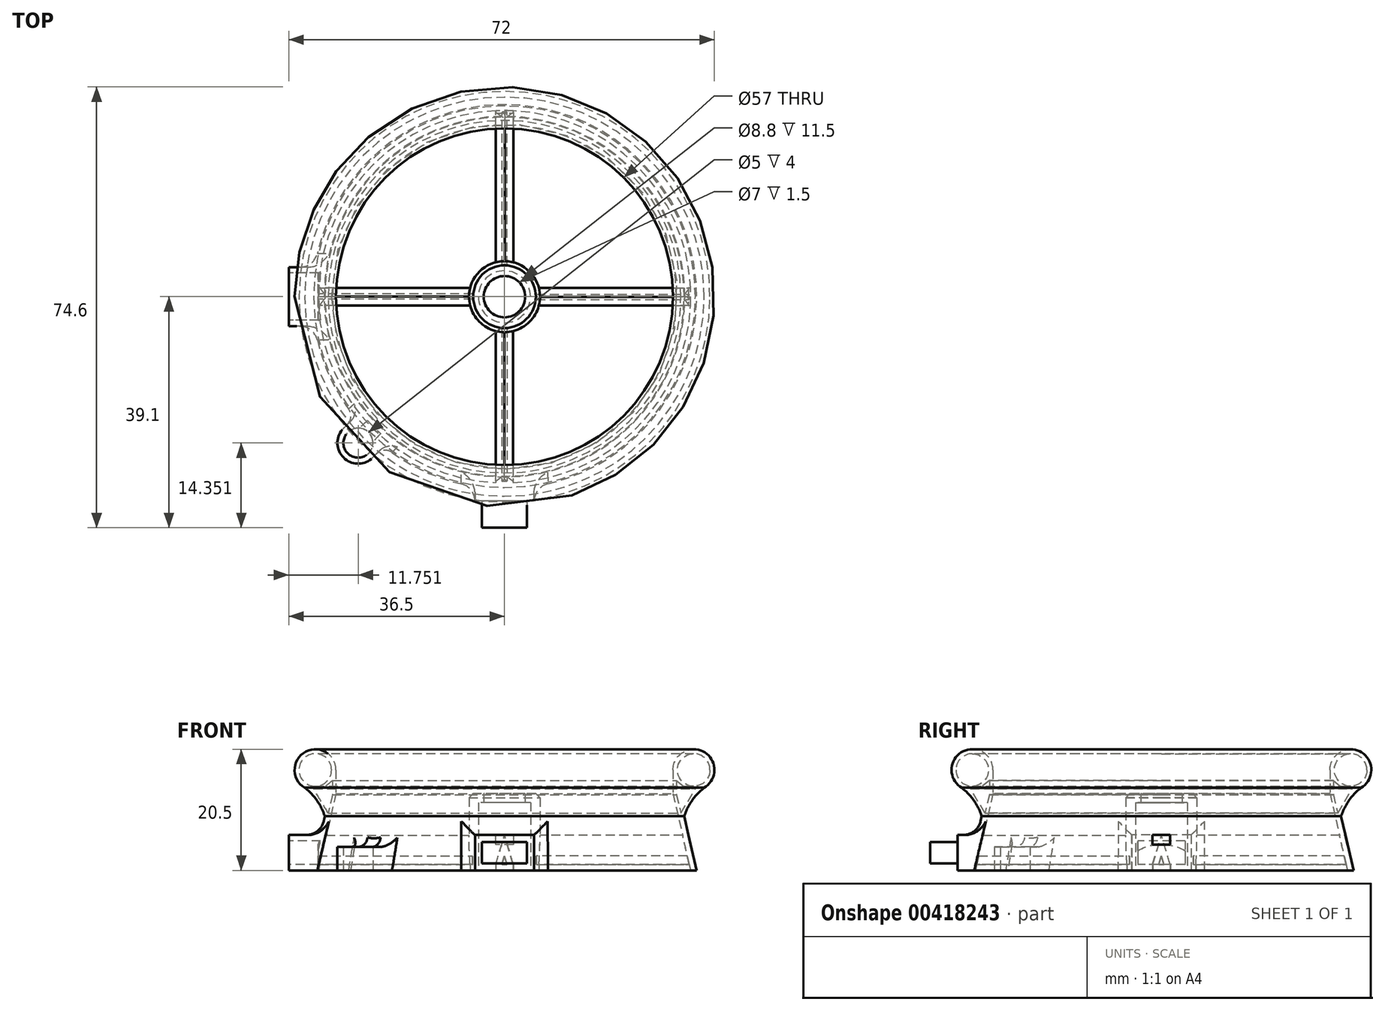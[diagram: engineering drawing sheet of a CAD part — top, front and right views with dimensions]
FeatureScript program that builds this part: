
annotation { "Feature Type Name" : "Feature", "Feature Type Description" : "" }
export const myFeature = defineFeature(function(context is Context, id is Id, definition is map)
    precondition{}
    {
        {
            var Q0;
            Q0=qCreatedBy(makeId("Top.planeOp"),FACE);
            var sketch = newSketch(context, id + "F0", { "sketchPlane" : qUnion([Q0])});
            skCircle(sketch, "E0", {"center": v(0, 0) * mm, "radius": 31.5 * mm});
            skCircle(sketch, "E1", {"center": v(0, 0) * mm, "radius": 4.4 * mm});
            skCircle(sketch, "E2", {"center": v(0, 0) * mm, "radius": 6 * mm});
            skLineSegment(sketch, "E3", {"start": v(5.82, 1.46) * mm, "end": v(31.47, 1.46) * mm});
            skLineSegment(sketch, "E4.MirrorCS", {"start": v(5.8, -1.5) * mm, "end": v(31.46, -1.5) * mm});
            skLineSegment(sketch, "E5.1.0", {"start": v(-1.46, 5.82) * mm, "end": v(-1.46, 31.47) * mm});
            skLineSegment(sketch, "E5.1.1", {"start": v(1.5, 5.8) * mm, "end": v(1.5, 31.46) * mm});
            skLineSegment(sketch, "E5.2.0", {"start": v(-5.82, -1.46) * mm, "end": v(-31.47, -1.46) * mm});
            skLineSegment(sketch, "E5.2.1", {"start": v(-5.8, 1.5) * mm, "end": v(-31.46, 1.5) * mm});
            skLineSegment(sketch, "E5.3.0", {"start": v(1.46, -5.82) * mm, "end": v(1.46, -31.47) * mm});
            skLineSegment(sketch, "E5.3.1", {"start": v(-1.5, -5.8) * mm, "end": v(-1.5, -31.46) * mm});
            skPoint(sketch, "E6.orphan", {"position": v(28.46, -1.5) * mm});
            skPoint(sketch, "E7.orphan", {"position": v(1.5, 28.46) * mm});
            skLineSegment(sketch, "E8", {"start": v(-31.1, 5) * mm, "end": v(-36.5, 5) * mm});
            skLineSegment(sketch, "E9.MirrorCS", {"start": v(-31.1, -5) * mm, "end": v(-36.5, -5) * mm});
            skLineSegment(sketch, "E10", {"start": v(-36.5, 5) * mm, "end": v(-36.5, -5) * mm});
            skPoint(sketch, "E11", {"position": v(-31.5, 0) * mm});
            skPoint(sketch, "E12", {"position": v(0, -31.5) * mm});
            skLineSegment(sketch, "E13", {"start": v(-5, -34.5) * mm, "end": v(-5, -31.1) * mm});
            skLineSegment(sketch, "E14.MirrorCS", {"start": v(5, -34.5) * mm, "end": v(5, -31.1) * mm});
            skLineSegment(sketch, "E15", {"start": v(-5, -34.5) * mm, "end": v(5, -34.5) * mm});
            skLineSegment(sketch, "E16", {"start": v(-3.8, -34.5) * mm, "end": v(-3.8, -39.1) * mm});
            skLineSegment(sketch, "E17.MirrorCS", {"start": v(3.8, -34.5) * mm, "end": v(3.8, -39.1) * mm});
            skLineSegment(sketch, "E18", {"start": v(-3.8, -39.1) * mm, "end": v(3.8, -39.1) * mm});
            skLineSegment(sketch, "E19", {"start": v(0, 0) * mm, "end": v(-4.24, -4.24) * mm});
            skPoint(sketch, "E20", {"position": v(-22.27, -22.27) * mm});
            skCircle(sketch, "E21", {"center": v(-24.75, -24.75) * mm, "radius": 2.5 * mm});
            skArc(sketch, "E22", {"start": v(-27.22, -22.27) * mm, "mid": v(-27.22, -27.22) * mm, "end": v(-22.27, -27.22) * mm});
            skPoint(sketch, "E23", {"position": v(-22.27, -27.22) * mm});
            skPoint(sketch, "E24", {"position": v(-27.22, -22.27) * mm});
            skLineSegment(sketch, "E25", {"start": v(-22.27, -27.22) * mm, "end": v(-19.66, -24.61) * mm});
            skLineSegment(sketch, "E26", {"start": v(-27.22, -22.27) * mm, "end": v(-24.61, -19.66) * mm});
            skSolve(sketch);
        }
        {
            var Q0;
            Q0=qCreatedBy(makeId("Front.planeOp"),FACE);
            var sketch = newSketch(context, id + "F1", { "sketchPlane" : qUnion([Q0])});
            skLineSegment(sketch, "E27", {"start": v(-27.5, 0) * mm, "end": v(-27.5, 17) * mm});
            skLineSegment(sketch, "E28", {"start": v(-28.5, 17) * mm, "end": v(-28.5, 13) * mm});
            skLineSegment(sketch, "E29", {"start": v(-28.5, 13) * mm, "end": v(-31.5, 0) * mm});
            skPoint(sketch, "E30.orphan", {"position": v(-28.5, 0) * mm});
            skArc(sketch, "E31", {"start": v(-28.5, 17) * mm, "mid": v(-33.74, 20.04) * mm, "end": v(-33.77, 13.98) * mm});
            skLineSegment(sketch, "E32", {"start": v(-31.5, 0) * mm, "end": v(-32.5, 0) * mm});
            skLineSegment(sketch, "E33", {"start": v(-32.5, 0) * mm, "end": v(-30.39, 9.15) * mm});
            skCircle(sketch, "E34", {"center": v(-32, 17) * mm, "radius": 2.75 * mm});
            skArc(sketch, "E35", {"start": v(-30.39, 9.15) * mm, "mid": v(-31.71, 11.82) * mm, "end": v(-33.77, 13.98) * mm});
            skLineSegment(sketch, "E36", {"start": v(-32.28, 13.8) * mm, "end": v(-29.83, 9.72) * mm});
            skLineSegment(sketch, "E37", {"start": v(-29.83, 9.72) * mm, "end": v(-29.08, 12.78) * mm});
            skLineSegment(sketch, "E38", {"start": v(-29.08, 12.78) * mm, "end": v(-29.08, 15.2) * mm});
            skLineSegment(sketch, "E39", {"start": v(-29.08, 15.2) * mm, "end": v(-30.51, 14.08) * mm});
            skLineSegment(sketch, "E40", {"start": v(-30.51, 14.08) * mm, "end": v(-32.28, 13.8) * mm});
            skLineSegment(sketch, "E41", {"start": v(-27.5, 0) * mm, "end": v(0, 0) * mm});
            skSolve(sketch);
        }
        {
            var Q0;
            Q0=makeQuery(id+"F1.imprint","IMPRINT",FACE,{"disambiguationData":[TD([[makeQuery(id+"F1.imprint","IMPRINT",EDGE,{"derivedFrom":sQuery(id+"F1.wireOp",EDGE,"E28")}),-1.0]])]});
            var Q1;
            Q1=sQuery(id+"F0.wireOp",EDGE,"E0");
            revolve(context, id + "F2", {"entities" : qUnion([Q0]), "axis" : qUnion([Q1]), "revolveType" : RevolveType.FULL});
        }
        {
            var Q0;
            {var subQ0=sQuery(id+"F0.wireOp",EDGE,"E5.2.0");Q0=makeQuery(id+"F0.imprint","IMPRINT",FACE,{"disambiguationData":[TD([[makeQuery(id+"F0.imprint","IMPRINT",EDGE,{"derivedFrom":subQ0}),-1.0]])]});}
            var Q1;
            {var subQ0=sQuery(id+"F0.wireOp",EDGE,"E5.3.0");Q1=makeQuery(id+"F0.imprint","IMPRINT",FACE,{"disambiguationData":[TD([[makeQuery(id+"F0.imprint","IMPRINT",EDGE,{"derivedFrom":subQ0}),-1.0]])]});}
            var Q2;
            {var subQ0=sQuery(id+"F0.wireOp",EDGE,"E3");Q2=makeQuery(id+"F0.imprint","IMPRINT",FACE,{"disambiguationData":[TD([[makeQuery(id+"F0.imprint","IMPRINT",EDGE,{"derivedFrom":subQ0}),-1.0]])]});}
            var Q3;
            {var subQ0=sQuery(id+"F0.wireOp",EDGE,"E5.1.0");Q3=makeQuery(id+"F0.imprint","IMPRINT",FACE,{"disambiguationData":[TD([[makeQuery(id+"F0.imprint","IMPRINT",EDGE,{"derivedFrom":subQ0}),-1.0]])]});}
            extrude(context, id + "F3", {"entities" : qUnion([Q0, Q1, Q2, Q3]), "operationType" : NewBodyOperationType.ADD, "depth" : 6 * mm});
        }
        {
            var Q0;
            Q0=makeQuery(id+"F0.imprint","IMPRINT",FACE,{"disambiguationData":[TD([[makeQuery(id+"F0.imprint","IMPRINT",EDGE,{"derivedFrom":sQuery(id+"F0.wireOp",EDGE,"E1")}),-1.0]])]});
            extrude(context, id + "F4", {"entities" : qUnion([Q0]), "operationType" : NewBodyOperationType.ADD, "depth" : 11.5 * mm});
        }
        {
            var Q0;
            {var subQ1=sQuery(id+"F0.wireOp",EDGE,"E5.3.0");Q0=makeQuery(id+"F3.boolean.opBoolean","SPLIT",EDGE,{"disambiguationData":[TD([makeQuery(id+"F2.opRevolve","SWEPT_FACE",FACE,{"disambiguationData":[OSD([sQuery(id+"F1.wireOp",EDGE,"E29")])]})])],"derivedFrom":makeQuery(id+"F3.opExtrude","CAP_EDGE",EDGE,{"disambiguationData":[OSD([subQ1])],"isStart":false})});}
            var Q1;
            {var subQ0=sQuery(id+"F0.wireOp",EDGE,"E3");Q1=makeQuery(id+"F3.boolean.opBoolean","SPLIT",EDGE,{"disambiguationData":[TD([makeQuery(id+"F2.opRevolve","SWEPT_FACE",FACE,{"disambiguationData":[OSD([sQuery(id+"F1.wireOp",EDGE,"E29")])]})])],"derivedFrom":makeQuery(id+"F3.opExtrude","CAP_EDGE",EDGE,{"disambiguationData":[OSD([subQ0])],"isStart":false})});}
            var Q2;
            {var subQ1=sQuery(id+"F0.wireOp",EDGE,"E5.1.0");Q2=makeQuery(id+"F3.boolean.opBoolean","SPLIT",EDGE,{"disambiguationData":[TD([makeQuery(id+"F2.opRevolve","SWEPT_FACE",FACE,{"disambiguationData":[OSD([sQuery(id+"F1.wireOp",EDGE,"E29")])]})])],"derivedFrom":makeQuery(id+"F3.opExtrude","CAP_EDGE",EDGE,{"disambiguationData":[OSD([subQ1])],"isStart":false})});}
            var Q3;
            {var subQ1=sQuery(id+"F0.wireOp",EDGE,"E5.2.0");Q3=makeQuery(id+"F3.boolean.opBoolean","SPLIT",EDGE,{"disambiguationData":[TD([makeQuery(id+"F2.opRevolve","SWEPT_FACE",FACE,{"disambiguationData":[OSD([sQuery(id+"F1.wireOp",EDGE,"E29")])]})])],"derivedFrom":makeQuery(id+"F3.opExtrude","CAP_EDGE",EDGE,{"disambiguationData":[OSD([subQ1])],"isStart":false})});}
            chamfer(context, id + "F5", {"entities" : qUnion([Q0, Q1, Q2, Q3]), "chamferType" : ChamferType.TWO_OFFSETS, "width1" : 1.5 * mm, "oppositeDirection" : true, "width2" : 5 * mm, "tangentPropagation" : true});
        }
        {
            var Q0;
            {var subQ2=sQuery(id+"F0.wireOp",EDGE,"E4.MirrorCS");Q0=makeQuery(id+"F3.boolean.opBoolean","SPLIT",EDGE,{"disambiguationData":[TD([makeQuery(id+"F2.opRevolve","SWEPT_FACE",FACE,{"disambiguationData":[OSD([sQuery(id+"F1.wireOp",EDGE,"E29")])]})])],"derivedFrom":makeQuery(id+"F3.opExtrude","CAP_EDGE",EDGE,{"disambiguationData":[OSD([subQ2])],"isStart":false})});}
            var Q1;
            {var subQ0=sQuery(id+"F0.wireOp",EDGE,"E5.1.1");Q1=makeQuery(id+"F3.boolean.opBoolean","SPLIT",EDGE,{"disambiguationData":[TD([makeQuery(id+"F2.opRevolve","SWEPT_FACE",FACE,{"disambiguationData":[OSD([sQuery(id+"F1.wireOp",EDGE,"E29")])]})])],"derivedFrom":makeQuery(id+"F3.opExtrude","CAP_EDGE",EDGE,{"disambiguationData":[OSD([subQ0])],"isStart":false})});}
            var Q2;
            {var subQ0=sQuery(id+"F0.wireOp",EDGE,"E5.3.1");Q2=makeQuery(id+"F3.boolean.opBoolean","SPLIT",EDGE,{"disambiguationData":[TD([makeQuery(id+"F2.opRevolve","SWEPT_FACE",FACE,{"disambiguationData":[OSD([sQuery(id+"F1.wireOp",EDGE,"E29")])]})])],"derivedFrom":makeQuery(id+"F3.opExtrude","CAP_EDGE",EDGE,{"disambiguationData":[OSD([subQ0])],"isStart":false})});}
            var Q3;
            {var subQ0=sQuery(id+"F0.wireOp",EDGE,"E5.2.1");Q3=makeQuery(id+"F3.boolean.opBoolean","SPLIT",EDGE,{"disambiguationData":[TD([makeQuery(id+"F2.opRevolve","SWEPT_FACE",FACE,{"disambiguationData":[OSD([sQuery(id+"F1.wireOp",EDGE,"E29")])]})])],"derivedFrom":makeQuery(id+"F3.opExtrude","CAP_EDGE",EDGE,{"disambiguationData":[OSD([subQ0])],"isStart":false})});}
            chamfer(context, id + "F6", {"entities" : qUnion([Q0, Q1, Q2, Q3]), "chamferType" : ChamferType.TWO_OFFSETS, "width1" : 5 * mm, "oppositeDirection" : true, "width2" : 1.5 * mm, "tangentPropagation" : true});
        }
        {
            var Q0;
            {var subQ0=sQuery(id+"F0.wireOp",EDGE,"E3");Q0=makeQuery(id+"F3.boolean.opBoolean","SPLIT",FACE,{"disambiguationData":[TD([makeQuery(id+"F2.opRevolve","SWEPT_FACE",FACE,{"disambiguationData":[OSD([sQuery(id+"F1.wireOp",EDGE,"E33")])]})])],"derivedFrom":makeQuery(id+"F3.opExtrude","SWEPT_FACE",FACE,{"disambiguationData":[OSD([subQ0])]})});}
            var Q1;
            Q1=sQuery(id+"F0.wireOp",EDGE,"E0");
            revolve(context, id + "F7", {"operationType" : NewBodyOperationType.REMOVE, "entities" : qUnion([Q0]), "axis" : qUnion([Q1]), "revolveType" : RevolveType.FULL, "oppositeDirection" : true});
        }
        {
            var Q0;
            {var subQ0=sQuery(id+"F0.wireOp",EDGE,"E8");Q0=makeQuery(id+"F0.imprint","IMPRINT",FACE,{"disambiguationData":[TD([[makeQuery(id+"F0.imprint","IMPRINT",EDGE,{"derivedFrom":subQ0}),1.0]])]});}
            extrude(context, id + "F8", {"entities" : qUnion([Q0]), "operationType" : NewBodyOperationType.ADD, "depth" : 6 * mm});
        }
        {
            var Q0;
            Q0=makeQuery(id+"F8.opExtrude","CAP_FACE",FACE,{"disambiguationData":[OSD([sQuery(id+"F0.wireOp",EDGE,"E0"),sQuery(id+"F0.wireOp",EDGE,"E8"),sQuery(id+"F0.wireOp",EDGE,"E9.MirrorCS"),sQuery(id+"F0.wireOp",EDGE,"E10")])],"isStart":false});
            var sketch = newSketch(context, id + "F9", { "sketchPlane" : qUnion([Q0])});
            skLineSegment(sketch, "E42", {"start": v(-34.09, 5) * mm, "end": v(-34.09, -5) * mm});
            skSolve(sketch);
        }
        {
            var Q0;
            {var subQ0=sQuery(id+"F9.wireOp",EDGE,"E42");Q0=makeQuery(id+"F9.imprint","IMPRINT",FACE,{"disambiguationData":[TD([[makeQuery(id+"F9.imprint","IMPRINT",EDGE,{"derivedFrom":subQ0}),1.0]])]});}
            extrude(context, id + "F10", {"entities" : qUnion([Q0]), "operationType" : NewBodyOperationType.REMOVE, "oppositeDirection" : true, "depth" : 2 * mm});
        }
        {
            var Q0;
            Q0=makeQuery(id+"F10.boolean.opBoolean","COPY",FACE,{"derivedFrom":makeQuery(id+"F10.opExtrude","SWEPT_FACE",FACE,{"disambiguationData":[OSD([sQuery(id+"F9.wireOp",EDGE,"E42")])]})});
            var Q1;
            Q1=makeQuery(id+"F2.opRevolve","SWEPT_BODY",BODY,{"disambiguationData":[OSD([sQuery(id+"F1.wireOp",EDGE,"E28"),sQuery(id+"F1.wireOp",EDGE,"E29"),sQuery(id+"F1.wireOp",EDGE,"E31"),sQuery(id+"F1.wireOp",EDGE,"E32"),sQuery(id+"F1.wireOp",EDGE,"E33"),sQuery(id+"F1.wireOp",EDGE,"E34"),sQuery(id+"F1.wireOp",EDGE,"E35"),sQuery(id+"F1.wireOp",EDGE,"E36"),sQuery(id+"F1.wireOp",EDGE,"E37"),sQuery(id+"F1.wireOp",EDGE,"E38"),sQuery(id+"F1.wireOp",EDGE,"E39"),sQuery(id+"F1.wireOp",EDGE,"E40")])]});
            extrude(context, id + "F11", {"entities" : qUnion([Q0]), "operationType" : NewBodyOperationType.ADD, "endBound" : BoundingType.UP_TO_BODY, "endBoundEntityBody" : qUnion([Q1]), "depth" : 25 * mm});
        }
        {
            var Q0;
            Q0=makeQuery(id+"F8.opExtrude","SWEPT_FACE",FACE,{"disambiguationData":[OSD([sQuery(id+"F0.wireOp",EDGE,"E10")])]});
            shell(context, id + "F12", {"entities" : qUnion([Q0]), "thickness" : 1 * mm});
        }
        {
            var Q0;
            {var subQ4=sQuery(id+"F0.wireOp",EDGE,"E13");Q0=makeQuery(id+"F0.imprint","IMPRINT",FACE,{"disambiguationData":[TD([[makeQuery(id+"F0.imprint","IMPRINT",EDGE,{"derivedFrom":subQ4}),-1.0]])]});}
            extrude(context, id + "F13", {"entities" : qUnion([Q0]), "operationType" : NewBodyOperationType.ADD, "depth" : 6 * mm});
        }
        {
            var Q0;
            Q0=makeQuery(id+"F13.opExtrude","CAP_FACE",FACE,{"disambiguationData":[OSD([sQuery(id+"F0.wireOp",EDGE,"E0"),sQuery(id+"F0.wireOp",EDGE,"E13"),sQuery(id+"F0.wireOp",EDGE,"E14.MirrorCS"),sQuery(id+"F0.wireOp",EDGE,"E15")])],"isStart":false});
            var sketch = newSketch(context, id + "F14", { "sketchPlane" : qUnion([Q0])});
            skLineSegment(sketch, "E43", {"start": v(-5, -32.8) * mm, "end": v(5, -32.8) * mm});
            skSolve(sketch);
        }
        {
            var Q0;
            {var subQ0=sQuery(id+"F14.wireOp",EDGE,"E43");Q0=makeQuery(id+"F14.imprint","IMPRINT",FACE,{"disambiguationData":[TD([[makeQuery(id+"F14.imprint","IMPRINT",EDGE,{"derivedFrom":subQ0}),1.0]])]});}
            extrude(context, id + "F15", {"entities" : qUnion([Q0]), "operationType" : NewBodyOperationType.REMOVE, "oppositeDirection" : true, "depth" : 2 * mm});
        }
        {
            var Q0;
            Q0=makeQuery(id+"F15.boolean.opBoolean","COPY",FACE,{"derivedFrom":makeQuery(id+"F15.opExtrude","SWEPT_FACE",FACE,{"disambiguationData":[OSD([sQuery(id+"F14.wireOp",EDGE,"E43")])]})});
            var Q1;
            Q1=makeQuery(id+"F2.opRevolve","SWEPT_BODY",BODY,{"disambiguationData":[OSD([sQuery(id+"F1.wireOp",EDGE,"E28"),sQuery(id+"F1.wireOp",EDGE,"E29"),sQuery(id+"F1.wireOp",EDGE,"E31"),sQuery(id+"F1.wireOp",EDGE,"E32"),sQuery(id+"F1.wireOp",EDGE,"E33"),sQuery(id+"F1.wireOp",EDGE,"E34"),sQuery(id+"F1.wireOp",EDGE,"E35"),sQuery(id+"F1.wireOp",EDGE,"E36"),sQuery(id+"F1.wireOp",EDGE,"E37"),sQuery(id+"F1.wireOp",EDGE,"E38"),sQuery(id+"F1.wireOp",EDGE,"E39"),sQuery(id+"F1.wireOp",EDGE,"E40")])]});
            extrude(context, id + "F16", {"entities" : qUnion([Q0]), "operationType" : NewBodyOperationType.ADD, "endBound" : BoundingType.UP_TO_BODY, "endBoundEntityBody" : qUnion([Q1]), "depth" : 25 * mm});
        }
        {
            var Q0;
            {var subQ0=sQuery(id+"F0.wireOp",EDGE,"E16");Q0=makeQuery(id+"F0.imprint","IMPRINT",FACE,{"disambiguationData":[TD([[makeQuery(id+"F0.imprint","IMPRINT",EDGE,{"derivedFrom":subQ0}),1.0]])]});}
            extrude(context, id + "F17", {"entities" : qUnion([Q0]), "operationType" : NewBodyOperationType.ADD, "depth" : 4.8 * mm, "hasSecondDirection" : true, "secondDirectionOppositeDirection" : false, "secondDirectionDepth" : 1.2 * mm});
        }
        {
            var Q0;
            {var subQ0=sQuery(id+"F0.wireOp",EDGE,"E9.MirrorCS");var subQ1=makeQuery(id+"F2.opRevolve","SWEPT_FACE",FACE,{"disambiguationData":[OSD([sQuery(id+"F1.wireOp",EDGE,"E33")])]});var subQ2=subQ1;var subQ3=makeQuery(id+"F8.opExtrude","SWEPT_FACE",FACE,{"disambiguationData":[OSD([subQ0])]});var subQ4=makeQuery(id+"F8.boolean.opBoolean","INTERSECT",EDGE,{"derivedFrom":[subQ2,subQ3]});Q0=makeQuery(id+"F11.boolean.opBoolean","MERGE",EDGE,{"derivedFrom":[makeQuery(id+"F10.boolean.opBoolean","SPLIT",EDGE,{"disambiguationData":[topologyDisambiguationEdgeConnected([subQ3])],"derivedFrom":subQ4}),makeQuery(id+"F10.boolean.opBoolean","SPLIT",EDGE,{"disambiguationData":[topologyDisambiguationEdgeConnected([makeQuery(id+"F10.opExtrude","SWEPT_FACE",FACE,{"disambiguationData":[OSD([subQ0])]})])],"derivedFrom":subQ4}),makeQuery(id+"F11.opExtrude","TWEAK_EDGE",EDGE,{"derivedFrom":[subQ2,makeQuery(id+"F10.boolean.opBoolean","COPY",EDGE,{"derivedFrom":makeQuery(id+"F10.opExtrude","SWEPT_EDGE",EDGE,{"disambiguationData":[OSD([subQ0,sQuery(id+"F9.wireOp",EDGE,"E42")])]})})]})]});}
            var Q1;
            {var subQ0=sQuery(id+"F1.wireOp",EDGE,"E33");var subQ1=sQuery(id+"F0.wireOp",EDGE,"E5.2.1");var subQ2=sQuery(id+"F0.wireOp",EDGE,"E5.2.0");var subQ3=sQuery(id+"F0.wireOp",EDGE,"E4.MirrorCS");var subQ4=sQuery(id+"F0.wireOp",EDGE,"E3");var subQ5=sQuery(id+"F0.wireOp",EDGE,"E2");var subQ6=sQuery(id+"F0.wireOp",EDGE,"E0");Q1=makeQuery(id+"F11.boolean.opBoolean","MERGE",EDGE,{"derivedFrom":[makeQuery(id+"F7.boolean.opBoolean","MERGE",EDGE,{"derivedFrom":[makeQuery(id+"F3.boolean.opBoolean","INTERSECT",EDGE,{"derivedFrom":[makeQuery(id+"F2.opRevolve","SWEPT_FACE",FACE,{"disambiguationData":[OSD([subQ0])]}),makeQuery(id+"F3.opExtrude","CAP_FACE",FACE,{"disambiguationData":[OSD([subQ6,subQ5,subQ2,subQ1])],"isStart":false})]}),makeQuery(id+"F7.opRevolve","SWEPT_EDGE",EDGE,{"disambiguationData":[OSD([subQ6,subQ5,subQ4,subQ3,subQ0])]})]}),makeQuery(id+"F11.opExtrude","CAP_EDGE",EDGE,{"disambiguationData":[OSD([subQ6,subQ5,subQ4,subQ3,subQ2,subQ1,subQ0])],"isStart":false})]});}
            var Q2;
            {var subQ0=sQuery(id+"F0.wireOp",EDGE,"E8");var subQ1=makeQuery(id+"F2.opRevolve","SWEPT_FACE",FACE,{"disambiguationData":[OSD([sQuery(id+"F1.wireOp",EDGE,"E33")])]});var subQ2=subQ1;var subQ3=makeQuery(id+"F8.opExtrude","SWEPT_FACE",FACE,{"disambiguationData":[OSD([subQ0])]});var subQ4=makeQuery(id+"F8.boolean.opBoolean","INTERSECT",EDGE,{"derivedFrom":[subQ2,subQ3]});Q2=makeQuery(id+"F11.boolean.opBoolean","MERGE",EDGE,{"derivedFrom":[makeQuery(id+"F10.boolean.opBoolean","SPLIT",EDGE,{"disambiguationData":[topologyDisambiguationEdgeConnected([subQ3])],"derivedFrom":subQ4}),makeQuery(id+"F10.boolean.opBoolean","SPLIT",EDGE,{"disambiguationData":[topologyDisambiguationEdgeConnected([makeQuery(id+"F10.opExtrude","SWEPT_FACE",FACE,{"disambiguationData":[OSD([subQ0])]})])],"derivedFrom":subQ4}),makeQuery(id+"F11.opExtrude","TWEAK_EDGE",EDGE,{"derivedFrom":[subQ2,makeQuery(id+"F10.boolean.opBoolean","COPY",EDGE,{"derivedFrom":makeQuery(id+"F10.opExtrude","SWEPT_EDGE",EDGE,{"disambiguationData":[OSD([subQ0,sQuery(id+"F9.wireOp",EDGE,"E42")])]})})]})]});}
            var Q3;
            {var subQ0=sQuery(id+"F0.wireOp",EDGE,"E13");var subQ1=makeQuery(id+"F2.opRevolve","SWEPT_FACE",FACE,{"disambiguationData":[OSD([sQuery(id+"F1.wireOp",EDGE,"E33")])]});var subQ2=subQ1;var subQ3=makeQuery(id+"F13.opExtrude","SWEPT_FACE",FACE,{"disambiguationData":[OSD([subQ0])]});var subQ4=makeQuery(id+"F13.boolean.opBoolean","INTERSECT",EDGE,{"derivedFrom":[subQ2,subQ3]});Q3=makeQuery(id+"F16.boolean.opBoolean","MERGE",EDGE,{"derivedFrom":[makeQuery(id+"F15.boolean.opBoolean","SPLIT",EDGE,{"disambiguationData":[topologyDisambiguationEdgeConnected([subQ3])],"derivedFrom":subQ4}),makeQuery(id+"F15.boolean.opBoolean","SPLIT",EDGE,{"disambiguationData":[topologyDisambiguationEdgeConnected([makeQuery(id+"F15.opExtrude","SWEPT_FACE",FACE,{"disambiguationData":[OSD([subQ0])]})])],"derivedFrom":subQ4}),makeQuery(id+"F16.opExtrude","TWEAK_EDGE",EDGE,{"derivedFrom":[subQ2,makeQuery(id+"F15.boolean.opBoolean","COPY",EDGE,{"derivedFrom":makeQuery(id+"F15.opExtrude","SWEPT_EDGE",EDGE,{"disambiguationData":[OSD([subQ0,sQuery(id+"F14.wireOp",EDGE,"E43")])]})})]})]});}
            var Q4;
            {var subQ0=sQuery(id+"F1.wireOp",EDGE,"E33");var subQ1=sQuery(id+"F0.wireOp",EDGE,"E5.3.1");var subQ2=sQuery(id+"F0.wireOp",EDGE,"E5.3.0");var subQ3=sQuery(id+"F0.wireOp",EDGE,"E4.MirrorCS");var subQ4=sQuery(id+"F0.wireOp",EDGE,"E3");var subQ5=sQuery(id+"F0.wireOp",EDGE,"E2");var subQ6=sQuery(id+"F0.wireOp",EDGE,"E0");Q4=makeQuery(id+"F16.boolean.opBoolean","MERGE",EDGE,{"derivedFrom":[makeQuery(id+"F7.boolean.opBoolean","MERGE",EDGE,{"derivedFrom":[makeQuery(id+"F3.boolean.opBoolean","INTERSECT",EDGE,{"derivedFrom":[makeQuery(id+"F2.opRevolve","SWEPT_FACE",FACE,{"disambiguationData":[OSD([subQ0])]}),makeQuery(id+"F3.opExtrude","CAP_FACE",FACE,{"disambiguationData":[OSD([subQ6,subQ5,subQ2,subQ1])],"isStart":false})]}),makeQuery(id+"F7.opRevolve","SWEPT_EDGE",EDGE,{"disambiguationData":[OSD([subQ6,subQ5,subQ4,subQ3,subQ0])]})]}),makeQuery(id+"F16.opExtrude","CAP_EDGE",EDGE,{"disambiguationData":[OSD([subQ6,subQ5,subQ4,subQ3,subQ2,subQ1,subQ0])],"isStart":false})]});}
            var Q5;
            {var subQ0=sQuery(id+"F0.wireOp",EDGE,"E14.MirrorCS");var subQ1=makeQuery(id+"F2.opRevolve","SWEPT_FACE",FACE,{"disambiguationData":[OSD([sQuery(id+"F1.wireOp",EDGE,"E33")])]});var subQ2=subQ1;var subQ3=makeQuery(id+"F13.opExtrude","SWEPT_FACE",FACE,{"disambiguationData":[OSD([subQ0])]});var subQ4=makeQuery(id+"F13.boolean.opBoolean","INTERSECT",EDGE,{"derivedFrom":[subQ2,subQ3]});Q5=makeQuery(id+"F16.boolean.opBoolean","MERGE",EDGE,{"derivedFrom":[makeQuery(id+"F15.boolean.opBoolean","SPLIT",EDGE,{"disambiguationData":[topologyDisambiguationEdgeConnected([subQ3])],"derivedFrom":subQ4}),makeQuery(id+"F15.boolean.opBoolean","SPLIT",EDGE,{"disambiguationData":[topologyDisambiguationEdgeConnected([makeQuery(id+"F15.opExtrude","SWEPT_FACE",FACE,{"disambiguationData":[OSD([subQ0])]})])],"derivedFrom":subQ4}),makeQuery(id+"F16.opExtrude","TWEAK_EDGE",EDGE,{"derivedFrom":[subQ2,makeQuery(id+"F15.boolean.opBoolean","COPY",EDGE,{"derivedFrom":makeQuery(id+"F15.opExtrude","SWEPT_EDGE",EDGE,{"disambiguationData":[OSD([subQ0,sQuery(id+"F14.wireOp",EDGE,"E43")])]})})]})]});}
            fillet(context, id + "F18", {"entities" : qUnion([Q0, Q1, Q2, Q3, Q4, Q5]), "radius" : 3 * mm, "tangentPropagation" : true, "allowEdgeOverflow" : false});
        }
        {
            var Q0;
            Q0=makeQuery(id+"F8.opExtrude","SWEPT_FACE",FACE,{"disambiguationData":[OSD([sQuery(id+"F0.wireOp",EDGE,"E10")])]});
            var sketch = newSketch(context, id + "F19", { "sketchPlane" : qUnion([Q0])});
            skLineSegment(sketch, "E44", {"start": v(-4, 5) * mm, "end": v(4, 5) * mm});
            skLineSegment(sketch, "E45", {"start": v(4, 5) * mm, "end": v(4, 1) * mm});
            skLineSegment(sketch, "E46", {"start": v(4, 1) * mm, "end": v(-4, 1) * mm});
            skLineSegment(sketch, "E47", {"start": v(-4, 1) * mm, "end": v(-4, 5) * mm});
            skSolve(sketch);
        }
        {
            var Q0;
            Q0=makeQuery(id+"F19.imprint","IMPRINT",FACE,{"disambiguationData":[TD([[makeQuery(id+"F19.imprint","IMPRINT",EDGE,{"derivedFrom":sQuery(id+"F19.wireOp",EDGE,"E44")}),-1.0]])]});
            extrude(context, id + "F20", {"entities" : qUnion([Q0]), "operationType" : NewBodyOperationType.REMOVE, "oppositeDirection" : true, "depth" : 5 * mm});
        }
        {
            var Q0;
            Q0=makeQuery(id+"F0.imprint","IMPRINT",FACE,{"disambiguationData":[TD([[makeQuery(id+"F0.imprint","IMPRINT",EDGE,{"derivedFrom":sQuery(id+"F0.wireOp",EDGE,"E21")}),-1.0]])]});
            extrude(context, id + "F21", {"entities" : qUnion([Q0]), "operationType" : NewBodyOperationType.ADD, "depth" : 4 * mm});
        }
        {
            var Q0;
            Q0=makeQuery(id+"F21.boolean.opBoolean","INTERSECT",EDGE,{"derivedFrom":[makeQuery(id+"F2.opRevolve","SWEPT_FACE",FACE,{"disambiguationData":[OSD([sQuery(id+"F1.wireOp",EDGE,"E33")])]}),makeQuery(id+"F21.opExtrude","SWEPT_FACE",FACE,{"disambiguationData":[OSD([sQuery(id+"F0.wireOp",EDGE,"E25")])]})]});
            var Q1;
            Q1=makeQuery(id+"F21.boolean.opBoolean","INTERSECT",EDGE,{"derivedFrom":[makeQuery(id+"F2.opRevolve","SWEPT_FACE",FACE,{"disambiguationData":[OSD([sQuery(id+"F1.wireOp",EDGE,"E33")])]}),makeQuery(id+"F21.opExtrude","SWEPT_FACE",FACE,{"disambiguationData":[OSD([sQuery(id+"F0.wireOp",EDGE,"E26")])]})]});
            var Q2;
            Q2=makeQuery(id+"F21.boolean.opBoolean","INTERSECT",EDGE,{"derivedFrom":[makeQuery(id+"F2.opRevolve","SWEPT_FACE",FACE,{"disambiguationData":[OSD([sQuery(id+"F1.wireOp",EDGE,"E33")])]}),makeQuery(id+"F21.opExtrude","CAP_FACE",FACE,{"disambiguationData":[OSD([sQuery(id+"F0.wireOp",EDGE,"E0"),sQuery(id+"F0.wireOp",EDGE,"E21"),sQuery(id+"F0.wireOp",EDGE,"E22"),sQuery(id+"F0.wireOp",EDGE,"E25"),sQuery(id+"F0.wireOp",EDGE,"E26")])],"isStart":false})]});
            fillet(context, id + "F22", {"entities" : qUnion([Q0, Q1, Q2]), "radius" : 2 * mm, "tangentPropagation" : true, "allowEdgeOverflow" : false});
        }
        {
            var Q0;
            Q0=makeQuery(id+"F4.opExtrude","CAP_FACE",FACE,{"disambiguationData":[OSD([sQuery(id+"F0.wireOp",EDGE,"E1"),sQuery(id+"F0.wireOp",EDGE,"E2")])],"isStart":false});
            var sketch = newSketch(context, id + "F23", { "sketchPlane" : qUnion([Q0])});
            skCircle(sketch, "E48", {"center": v(0, 0) * mm, "radius": 3.5 * mm});
            skSolve(sketch);
        }
        {
            var Q0;
            Q0=makeQuery(id+"F23.imprint","IMPRINT",FACE,{"disambiguationData":[TD([[makeQuery(id+"F23.imprint","IMPRINT",EDGE,{"derivedFrom":sQuery(id+"F23.wireOp",EDGE,"E48")}),-1.0]])]});
            var Q1;
            Q1=makeQuery(id+"F23.imprint","IMPRINT",FACE,{"disambiguationData":[TD([[makeQuery(id+"F23.imprint","IMPRINT",EDGE,{"derivedFrom":makeQuery(id+"F4.opExtrude","CAP_EDGE",EDGE,{"disambiguationData":[OSD([sQuery(id+"F0.wireOp",EDGE,"E1")])],"isStart":false})}),-1.0]])]});
            extrude(context, id + "F24", {"entities" : qUnion([Q0, Q1]), "operationType" : NewBodyOperationType.ADD, "depth" : 1.5 * mm});
        }
        {
            var Q0;
            Q0=makeQuery(id+"F24.opExtrude","CAP_EDGE",EDGE,{"disambiguationData":[OSD([sQuery(id+"F0.wireOp",EDGE,"E2")])],"isStart":false});
            chamfer(context, id + "F25", {"entities" : qUnion([Q0]), "width" : 0.7 * mm, "tangentPropagation" : true});
        }
    });
